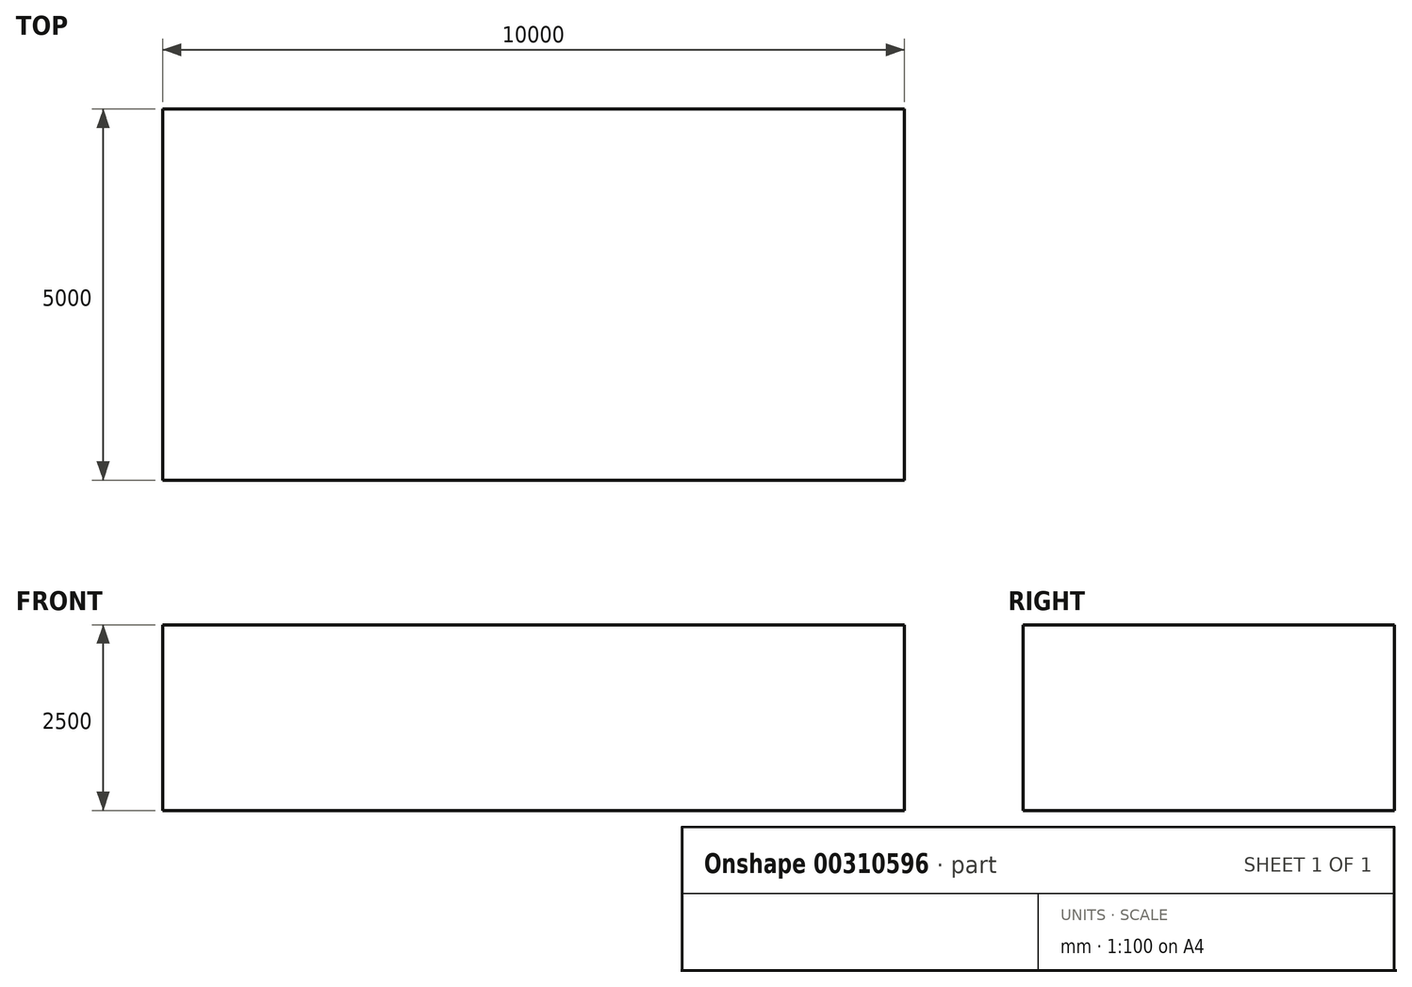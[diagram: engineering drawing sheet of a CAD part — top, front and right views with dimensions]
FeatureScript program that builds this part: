
annotation { "Feature Type Name" : "Feature", "Feature Type Description" : "" }
export const myFeature = defineFeature(function(context is Context, id is Id, definition is map)
    precondition{}
    {
        {
            var Q0;
            Q0=qCreatedBy(makeId("Front.planeOp"),FACE);
            var sketch = newSketch(context, id + "F0", { "sketchPlane" : qUnion([Q0])});
            skLineSegment(sketch, "E0.bottom", {"start": v(-2064.84, 1263.15) * mm, "end": v(7935.16, 1263.15) * mm});
            skLineSegment(sketch, "E0.top", {"start": v(-2064.84, -1236.85) * mm, "end": v(7935.16, -1236.85) * mm});
            skLineSegment(sketch, "E0.left", {"start": v(-2064.84, 1263.15) * mm, "end": v(-2064.84, -1236.85) * mm});
            skLineSegment(sketch, "E0.right", {"start": v(7935.16, 1263.15) * mm, "end": v(7935.16, -1236.85) * mm});
            skSolve(sketch);
        }
        {
            var Q0;
            Q0 = qSketchRegion(id + "F0", true);
            extrude(context, id + "F1", {"entities" : qUnion([Q0]), "depth" : 5000 * mm});
        }
    });
